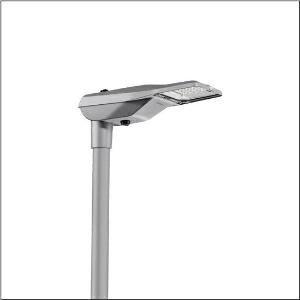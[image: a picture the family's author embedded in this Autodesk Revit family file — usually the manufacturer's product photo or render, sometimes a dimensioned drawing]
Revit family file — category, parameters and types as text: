
# Revit family: streetlight_sl_21_iq_micro___st1_0a_5xe1d61y08db_6c32
name_source: partatom
category: Lighting Fixtures
units: mm (PartAtom-declared; Revit-internal decimal feet)

## family parameters
Cut with Voids When Loaded = No
Host = Face
Light Source = No
Part Type = Normal
Room Calculation Point = No
Round Connector Dimension = Use Diameter
Shared = No

## types (1)
- --- (1 x LED, 4430 lm, 39.1 W, 2700K)
    Apparent Load = 39 VA
    CIE Flux Codes = 37 72 97 100 100
    Color Rendering = 70
    Color Temperature = 2700K
    Default Elevation = 1800 mm
    Description = Streetlight SL 21 iQ micro, mast luminaire, primary light control with lens, of PMMA, primary optical cover: cover, of toughened safety glass, transparent, light distribution: ST1.0a, light emission: direct distribution, primary light characteristic: asymmetric, installation type: post-top, side-entry, LED, High Power LED, rated luminous flux: 4.430lm, luminous efficacy: 113lm/W, light colour: 727, colour temperature: 2700K, control: presetting dimming logarithmic, Street-Remote, Auto-Match, Temp-Guard, Lumen-Switch, Night-Set, Smart-Wire, Light-Fading, Desk-Remote (wireless, voltage-free reading and setting of iQ features in the workshop via application-optimized NFC function/RFID function), optimised constant luminous flux control (CLO 2.0), mains connection: 220..240V, AC, 50/60Hz, start of lifetime: 39W, end of service life: 41W, reduction: 17W, luminaire housing, of diecast aluminium, powder-coated, Siteco® metallic grey (DB 702S), corrosivity category C5 mid according to DIN EN ISO 12944, please order mast flange separately, inclination adjustable: 0°, 5°, 10°, 15°, sealing non-destructively replaceable, multi-level sealing system, length: 528mm, width: 235mm, height: 110mm, mast flange for spigot size: 42mm (side-entry): 5XC10008XM4, 60/48mm (side-entry/post-top): 5XC10108XM2, 76/60mm (side-entry/post-top): 5XC10108XM1, Smart Interface below and above, protection rating (complete): IP66, insulation class (complete): insulation class II (safety insulation), certification: CE, ENEC, ENEC+, VDE, impact resistance: IK09, permissible operating ambient temperature for outdoor applications: -40..+50°C, standard-compliant lighting for roads and squares, packaging unit: 1 piece

Light Distribution: ST1.0a
    Height = 110 mm
    Lamp = 1 x LED
    Lamp Light Flux = 4430 lm
    Lamp Power = 39.1 W
    Lamp count = 1
    Length = 528 mm
    Luminous efficacy = 113 lm/W
    Manufacturer = Siteco
    ModVariant = No
    Model = 5XE1D61Y08DB
    Number of Poles = 1
    OnlyDefault = Yes
    Power Factor = 1
    Product Name = Streetlight SL 21 iQ micro | ST1.0a
    Product group = mast luminaire | pylon top
    ProductGroupID = 6100
    Protection Class = Protection class II
    Protection Degree = IP 66
    RLX_Detail_Level = 1
    RLX_Emergency_Light_Flux = 0 lm
    RLX_Emergency_Type = 0
    RLX_Emergency_Type_DB = No
    RlxData = <blob elided: 98841 chars, md5=e9eaea64>
    Socket = socket
    Standby Power = 0 W
    System Light Flux = 4430 lm
    System Power = 39 W
    Type Comments = factory setting: luminous flux: 100 % | dim-lin: 254 | 765 mA
    Type Image = l_1007239.jpg
    URL = http://relux.com
    VarID = @adj_045533
    Voltage = 0 V
    Weight = 0.00 kg
    Width = 235 mm

## geometry (parser evidence)
native form markers: Blend x4, Sweep x12
no freeform markers — native parametric forms only
